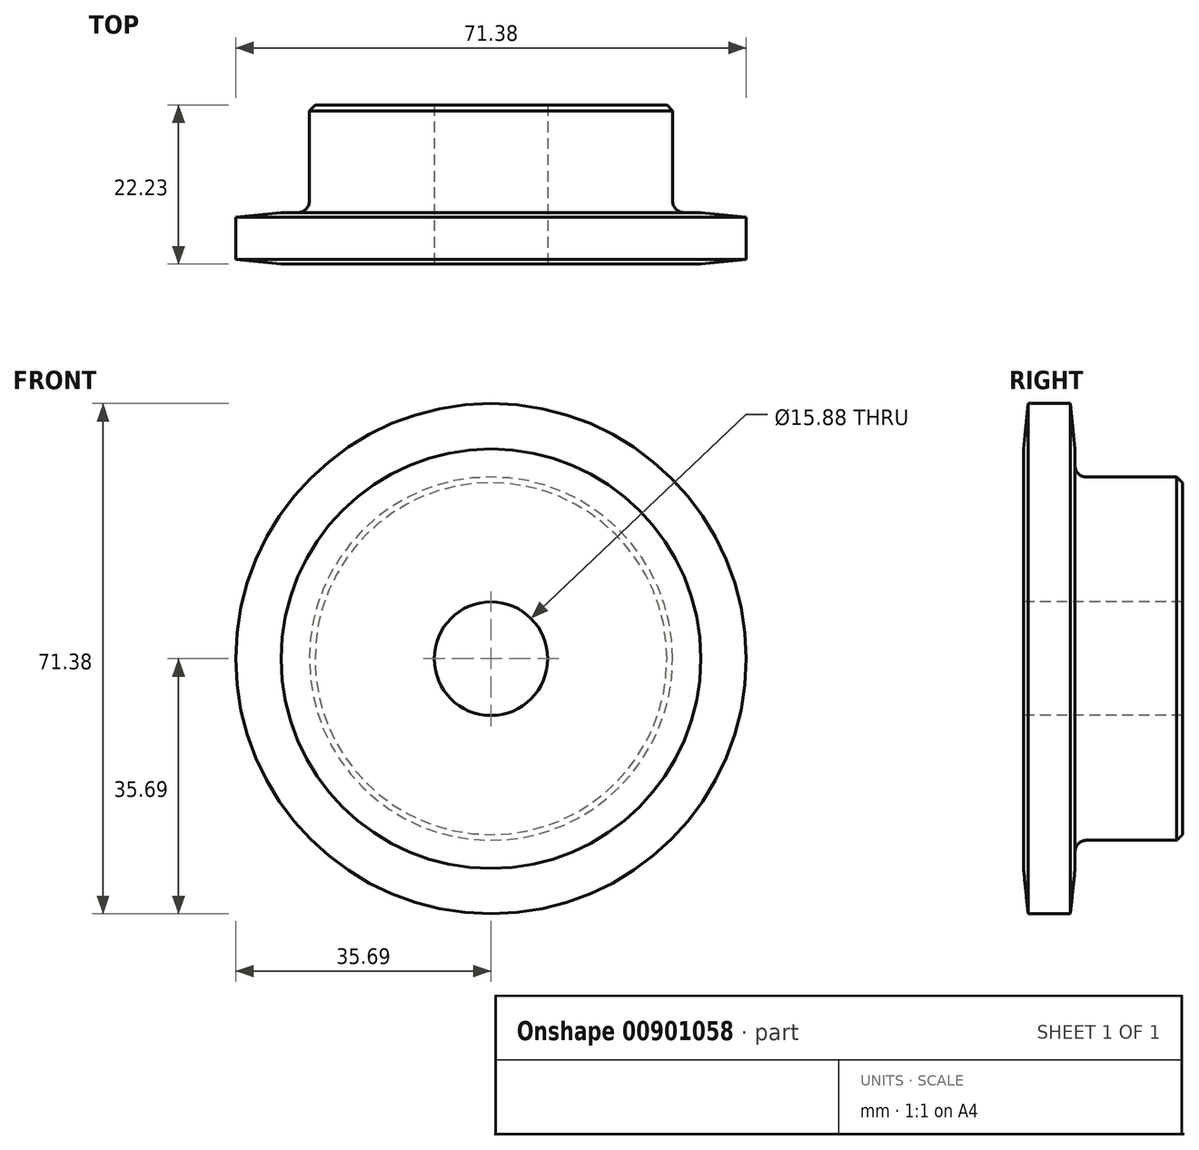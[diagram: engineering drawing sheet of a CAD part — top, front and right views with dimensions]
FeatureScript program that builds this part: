
annotation { "Feature Type Name" : "Feature", "Feature Type Description" : "" }
export const myFeature = defineFeature(function(context is Context, id is Id, definition is map)
    precondition{}
    {
        {
            var Q0;
            Q0=qCreatedBy(makeId("Right.planeOp"),FACE);
            var sketch = newSketch(context, id + "F0", { "sketchPlane" : qUnion([Q0])});
            skLineSegment(sketch, "E0", {"start": v(0, 0) * mm, "end": v(22.23, 0) * mm, "construction": true});
            skLineSegment(sketch, "E1.bottom", {"start": v(0, 7.94) * mm, "end": v(7.21, 7.94) * mm});
            skLineSegment(sketch, "E1.top", {"start": v(0, 35.69) * mm, "end": v(7.21, 35.69) * mm});
            skLineSegment(sketch, "E1.left", {"start": v(0, 7.94) * mm, "end": v(0, 35.69) * mm});
            skLineSegment(sketch, "E1.right", {"start": v(7.21, 7.94) * mm, "end": v(7.21, 35.69) * mm});
            skLineSegment(sketch, "E2.bottom", {"start": v(0, 7.94) * mm, "end": v(22.23, 7.94) * mm});
            skLineSegment(sketch, "E2.top", {"start": v(0, 25.4) * mm, "end": v(22.23, 25.4) * mm});
            skLineSegment(sketch, "E2.left", {"start": v(0, 7.94) * mm, "end": v(0, 25.4) * mm});
            skLineSegment(sketch, "E2.right", {"start": v(22.22, 7.94) * mm, "end": v(22.22, 25.4) * mm});
            skLineSegment(sketch, "E3.MirrorCS", {"start": v(0, -7.94) * mm, "end": v(7.21, -7.94) * mm});
            skLineSegment(sketch, "E4.MirrorCS", {"start": v(22.23, -7.94) * mm, "end": v(22.23, -25.4) * mm});
            skLineSegment(sketch, "E5.MirrorCS", {"start": v(0, -7.94) * mm, "end": v(22.23, -7.94) * mm});
            skLineSegment(sketch, "E6.MirrorCS", {"start": v(0, -7.94) * mm, "end": v(0, -25.4) * mm});
            skLineSegment(sketch, "E7.MirrorCS", {"start": v(0, -25.4) * mm, "end": v(22.23, -25.4) * mm});
            skLineSegment(sketch, "E8.MirrorCS", {"start": v(0, -7.94) * mm, "end": v(0, -35.69) * mm});
            skLineSegment(sketch, "E9.MirrorCS", {"start": v(0, -35.69) * mm, "end": v(7.21, -35.69) * mm});
            skLineSegment(sketch, "E10.MirrorCS", {"start": v(7.21, -7.94) * mm, "end": v(7.21, -35.69) * mm});
            skSolve(sketch);
        }
        {
            var Q0;
            {var subQ0=sQuery(id+"F0.wireOp",EDGE,"E2.bottom");Q0=makeQuery(id+"F0.imprint","IMPRINT",FACE,{"disambiguationData":[TD([[makeQuery(id+"F0.imprint","IMPRINT",EDGE,{"derivedFrom":subQ0}),1.0]])]});}
            var Q1;
            {var subQ0=sQuery(id+"F0.wireOp",EDGE,"E1.top");Q1=makeQuery(id+"F0.imprint","IMPRINT",FACE,{"disambiguationData":[TD([[makeQuery(id+"F0.imprint","IMPRINT",EDGE,{"derivedFrom":subQ0}),-1.0]])]});}
            var Q2;
            {var subQ0=sQuery(id+"F0.wireOp",EDGE,"E1.bottom");Q2=makeQuery(id+"F0.imprint","IMPRINT",FACE,{"disambiguationData":[TD([[makeQuery(id+"F0.imprint","IMPRINT",EDGE,{"derivedFrom":subQ0}),1.0]])]});}
            var Q3;
            Q3=sQuery(id+"F0.wireOp",EDGE,"E0");
            revolve(context, id + "F1", {"surfaceOperationType" : NewSurfaceOperationType.NEW, "entities" : qUnion([Q0, Q1, Q2]), "axis" : qUnion([Q3]), "revolveType" : RevolveType.FULL});
        }
        {
            var Q0;
            Q0=makeQuery(id+"F1.opRevolve","SWEPT_EDGE",EDGE,{"disambiguationData":[OSD([sQuery(id+"F0.wireOp",EDGE,"E1.right"),sQuery(id+"F0.wireOp",EDGE,"E2.top")])]});
            fillet(context, id + "F2", {"entities" : qUnion([Q0]), "radius" : 1.59 * mm, "tangentPropagation" : true, "allowEdgeOverflow" : false});
        }
        {
            var Q0;
            Q0=makeQuery(id+"F1.opRevolve","SWEPT_EDGE",EDGE,{"disambiguationData":[OSD([sQuery(id+"F0.wireOp",EDGE,"E2.top"),sQuery(id+"F0.wireOp",EDGE,"E2.right")])]});
            chamfer(context, id + "F3", {"entities" : qUnion([Q0]), "width" : 0.8 * mm, "tangentPropagation" : true});
        }
        {
            var Q0;
            Q0=makeQuery(id+"F1.opRevolve","SWEPT_EDGE",EDGE,{"disambiguationData":[OSD([sQuery(id+"F0.wireOp",EDGE,"E1.top"),sQuery(id+"F0.wireOp",EDGE,"E1.left")])]});
            var Q1;
            Q1=makeQuery(id+"F1.opRevolve","SWEPT_EDGE",EDGE,{"disambiguationData":[OSD([sQuery(id+"F0.wireOp",EDGE,"E1.top"),sQuery(id+"F0.wireOp",EDGE,"E1.right")])]});
            chamfer(context, id + "F4", {"entities" : qUnion([Q0, Q1]), "chamferType" : ChamferType.TWO_OFFSETS, "width1" : 6.35 * mm, "oppositeDirection" : false, "width2" : 0.66 * mm, "tangentPropagation" : true});
        }
    });
